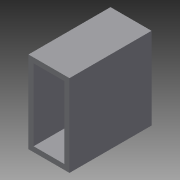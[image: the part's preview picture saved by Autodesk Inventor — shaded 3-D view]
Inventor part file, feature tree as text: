
AUTODESK INVENTOR PART (.ipt)
format: ipt  version: 2016 (Build 200138000, 138)  size: 77,824 bytes
history: native  units: in
note: dims shown in document units (in); Inventor stores cm internally (conversion verified against a paired STEP export)
features: extrude x1, sketch x1
ambient origin geometry x8: Origin, YZ Plane, XZ Plane, XY Plane, X Axis, Y Axis, Z Axis, Center Point
bodies: Solid1 (feature_tree)
feature tree (2):
  extrude  "Extrusion1"  Depth=2.0in
  sketch  "Sketch1"  dims[d0=1.0in d1=2.0in d2=0.125in d3=0.125in d4=0.125in d5=0.125in d6=2.0in d7=0.0in]
